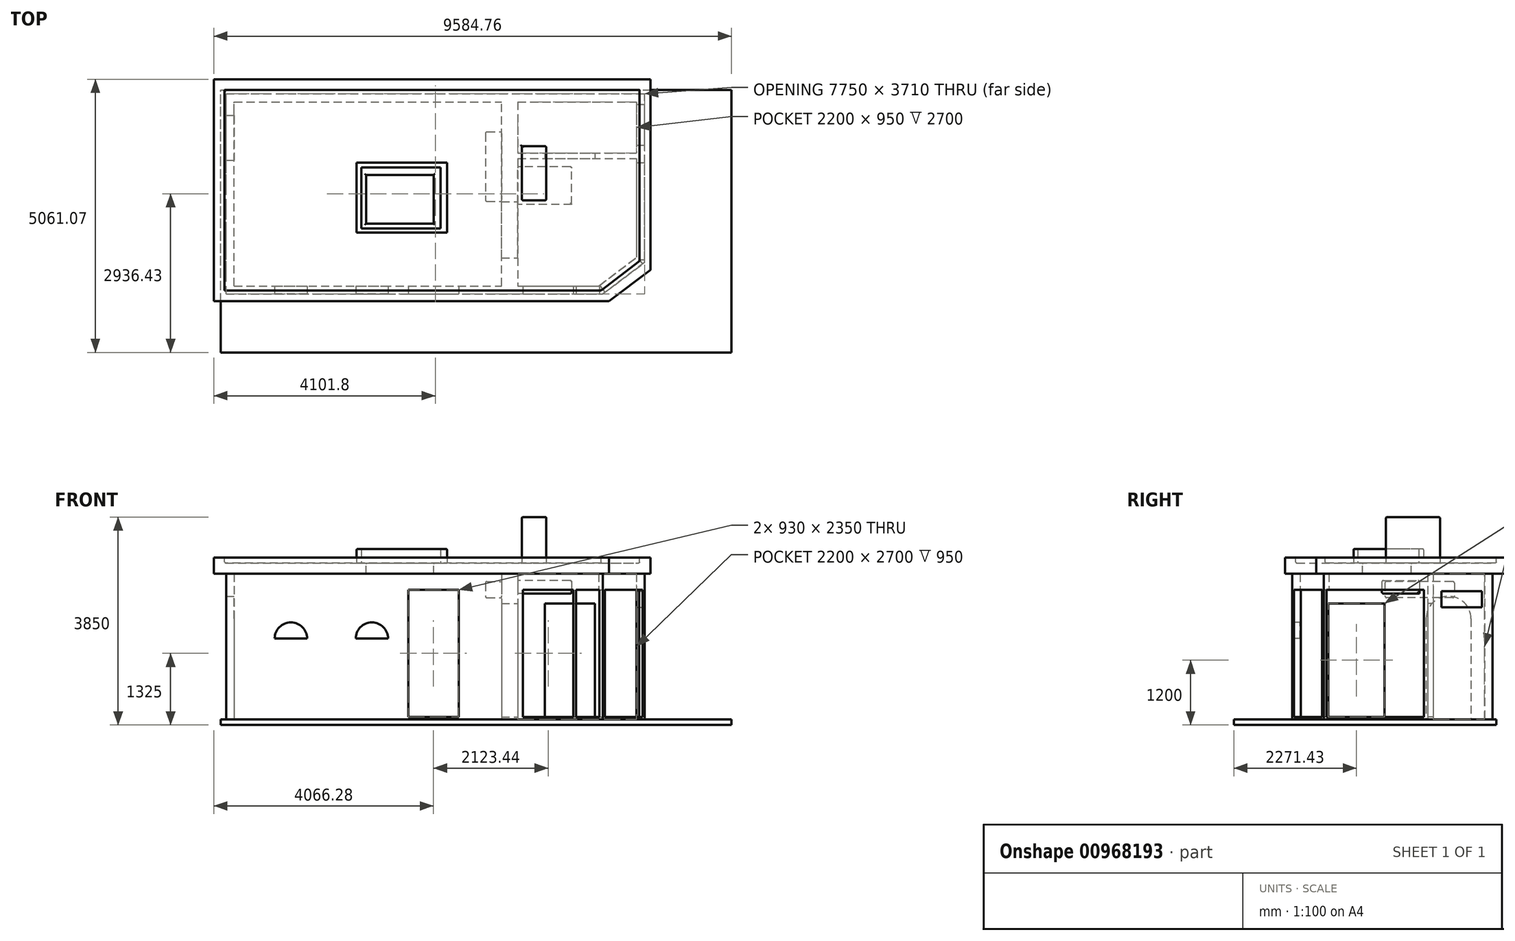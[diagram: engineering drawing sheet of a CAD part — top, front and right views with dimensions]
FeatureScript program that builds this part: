
annotation { "Feature Type Name" : "Feature", "Feature Type Description" : "" }
export const myFeature = defineFeature(function(context is Context, id is Id, definition is map)
    precondition{}
    {
        {
            var Q0;
            Q0=qCreatedBy(makeId("Top.planeOp"),FACE);
            var sketch = newSketch(context, id + "F0", { "sketchPlane" : qUnion([Q0])});
            skLineSegment(sketch, "E0.bottom", {"start": v(-3940.68, -1155.16) * mm, "end": v(1009.32, -1155.16) * mm});
            skLineSegment(sketch, "E0.top", {"start": v(-3940.68, 2254.84) * mm, "end": v(1009.32, 2254.84) * mm});
            skLineSegment(sketch, "E0.left", {"start": v(-3940.68, -1155.16) * mm, "end": v(-3940.68, 2254.84) * mm});
            skLineSegment(sketch, "E0.right", {"start": v(1009.32, -1155.16) * mm, "end": v(1009.32, 2254.84) * mm});
            skLineSegment(sketch, "E1.bottom", {"start": v(1309.32, 2254.84) * mm, "end": v(3509.32, 2254.84) * mm});
            skLineSegment(sketch, "E1.top", {"start": v(1309.32, -1155.16) * mm, "end": v(2809.32, -1155.16) * mm});
            skLineSegment(sketch, "E1.left", {"start": v(1309.32, 2254.84) * mm, "end": v(1309.32, -1155.16) * mm});
            skLineSegment(sketch, "E1.right", {"start": v(3509.32, 2254.84) * mm, "end": v(3509.32, -625.16) * mm});
            skLineSegment(sketch, "E2.bottom", {"start": v(-4090.68, -1305.16) * mm, "end": v(2885, -1305.16) * mm});
            skLineSegment(sketch, "E2.top", {"start": v(-4090.68, 2404.84) * mm, "end": v(3659.32, 2404.84) * mm});
            skLineSegment(sketch, "E2.left", {"start": v(-4090.68, -1305.16) * mm, "end": v(-4090.68, 2404.84) * mm});
            skLineSegment(sketch, "E2.right", {"start": v(3659.32, -718.9) * mm, "end": v(3659.32, 2404.84) * mm});
            skLineSegment(sketch, "E3", {"start": v(2809.32, -1155.16) * mm, "end": v(3509.32, -625.16) * mm});
            skPoint(sketch, "E4.orphan", {"position": v(3509.32, -1155.16) * mm});
            skLineSegment(sketch, "E5.bottom", {"start": v(1309.32, 1304.84) * mm, "end": v(1809.32, 1304.84) * mm});
            skLineSegment(sketch, "E5.top", {"start": v(1309.32, 1204.84) * mm, "end": v(1809.32, 1204.84) * mm});
            skLineSegment(sketch, "E5.left", {"start": v(1309.32, 1304.84) * mm, "end": v(1309.32, 1204.84) * mm});
            skLineSegment(sketch, "E6.right", {"start": v(3509.32, 1304.84) * mm, "end": v(3509.32, 1204.84) * mm});
            skPoint(sketch, "E7.orphan", {"position": v(1809.32, 1359.23) * mm});
            skLineSegment(sketch, "E8", {"start": v(3659.32, -718.9) * mm, "end": v(2885, -1305.16) * mm});
            skPoint(sketch, "E9.right.end.orphan", {"position": v(2739.32, 1204.84) * mm});
            skLineSegment(sketch, "E10", {"start": v(1809.32, 1304.84) * mm, "end": v(3509.32, 1304.84) * mm});
            skLineSegment(sketch, "E11", {"start": v(3509.32, 1204.84) * mm, "end": v(1809.32, 1204.84) * mm});
            skSolve(sketch);
        }
        {
            var Q0;
            Q0=makeQuery(id+"F0.imprint","IMPRINT",FACE,{"disambiguationData":[TD([[makeQuery(id+"F0.imprint","IMPRINT",EDGE,{"derivedFrom":sQuery(id+"F0.wireOp",EDGE,"E0.bottom")}),-1.0]])]});
            var Q1;
            Q1=makeQuery(id+"F0.imprint","IMPRINT",FACE,{"disambiguationData":[TD([[makeQuery(id+"F0.imprint","IMPRINT",EDGE,{"derivedFrom":sQuery(id+"F0.wireOp",EDGE,"E5.bottom")}),-1.0]])]});
            var Q2;
            Q2=makeQuery(id+"F0.imprint","IMPRINT",FACE,{"disambiguationData":[TD([[makeQuery(id+"F0.imprint","IMPRINT",EDGE,{"derivedFrom":sQuery(id+"F0.wireOp",EDGE,"E6.bottom")}),-1.0]])]});
            extrude(context, id + "F1", {"entities" : qUnion([Q0, Q1, Q2]), "depth" : 2700 * mm, "offsetDistance" : 25 * mm});
        }
        {
            var Q0;
            Q0=makeQuery(id+"F1.opExtrude","SWEPT_FACE",FACE,{"disambiguationData":[OSD([sQuery(id+"F0.wireOp",EDGE,"E2.bottom")])]});
            var sketch = newSketch(context, id + "F2", { "sketchPlane" : qUnion([Q0])});
            skLineSegment(sketch, "E12", {"start": v(-4012.93, 1500) * mm, "end": v(-3190.68, 1500) * mm, "construction": true});
            skArc(sketch, "E13", {"start": v(-2590.68, 1500) * mm, "mid": v(-2890.68, 1800) * mm, "end": v(-3190.68, 1500) * mm});
            skLineSegment(sketch, "E14", {"start": v(-3190.68, 1500) * mm, "end": v(-2590.68, 1500) * mm, "construction": true});
            skLineSegment(sketch, "E15", {"start": v(-2590.68, 1500) * mm, "end": v(902.67, 1500) * mm, "construction": true});
            skArc(sketch, "E16", {"start": v(-1090.68, 1500) * mm, "mid": v(-1390.68, 1800) * mm, "end": v(-1690.68, 1500) * mm});
            skLineSegment(sketch, "E17", {"start": v(-3190.68, 1500) * mm, "end": v(-2590.68, 1500) * mm});
            skLineSegment(sketch, "E18", {"start": v(-1690.68, 1500) * mm, "end": v(-1090.68, 1500) * mm});
            skLineSegment(sketch, "E19.bottom", {"start": v(-716.2, 2400) * mm, "end": v(213.8, 2400) * mm});
            skLineSegment(sketch, "E19.top", {"start": v(-716.2, 50) * mm, "end": v(213.8, 50) * mm});
            skLineSegment(sketch, "E19.left", {"start": v(-716.2, 2400) * mm, "end": v(-716.2, 50) * mm});
            skLineSegment(sketch, "E19.right", {"start": v(213.8, 2400) * mm, "end": v(213.8, 50) * mm});
            skLineSegment(sketch, "E20.bottom", {"start": v(1407.24, 2400) * mm, "end": v(2337.24, 2400) * mm});
            skLineSegment(sketch, "E20.top", {"start": v(1407.24, 50) * mm, "end": v(2337.24, 50) * mm});
            skLineSegment(sketch, "E20.left", {"start": v(1407.24, 2400) * mm, "end": v(1407.24, 50) * mm});
            skLineSegment(sketch, "E20.right", {"start": v(2337.24, 2400) * mm, "end": v(2337.24, 50) * mm});
            skLineSegment(sketch, "E21.bottom", {"start": v(2387.24, 2400) * mm, "end": v(2822.09, 2400) * mm});
            skLineSegment(sketch, "E21.top", {"start": v(2387.24, 50) * mm, "end": v(2822.09, 50) * mm});
            skLineSegment(sketch, "E21.left", {"start": v(2387.24, 2400) * mm, "end": v(2387.24, 50) * mm});
            skLineSegment(sketch, "E21.right", {"start": v(2822.09, 2400) * mm, "end": v(2822.09, 50) * mm});
            skSolve(sketch);
        }
        {
            var Q0;
            Q0=makeQuery(id+"F2.imprint","IMPRINT",FACE,{"disambiguationData":[TD([[makeQuery(id+"F2.imprint","IMPRINT",EDGE,{"derivedFrom":sQuery(id+"F2.wireOp",EDGE,"E16")}),1.0]])]});
            var Q1;
            Q1=makeQuery(id+"F2.imprint","IMPRINT",FACE,{"disambiguationData":[TD([[makeQuery(id+"F2.imprint","IMPRINT",EDGE,{"derivedFrom":sQuery(id+"F2.wireOp",EDGE,"E13")}),1.0]])]});
            var Q2;
            Q2=makeQuery(id+"F2.imprint","IMPRINT",FACE,{"disambiguationData":[TD([[makeQuery(id+"F2.imprint","IMPRINT",EDGE,{"derivedFrom":sQuery(id+"F2.wireOp",EDGE,"E19.bottom")}),-1.0]])]});
            var Q3;
            Q3=makeQuery(id+"F2.imprint","IMPRINT",FACE,{"disambiguationData":[TD([[makeQuery(id+"F2.imprint","IMPRINT",EDGE,{"derivedFrom":sQuery(id+"F2.wireOp",EDGE,"E21.bottom")}),-1.0]])]});
            var Q4;
            Q4=makeQuery(id+"F2.imprint","IMPRINT",FACE,{"disambiguationData":[TD([[makeQuery(id+"F2.imprint","IMPRINT",EDGE,{"derivedFrom":sQuery(id+"F2.wireOp",EDGE,"E20.bottom")}),-1.0]])]});
            extrude(context, id + "F3", {"entities" : qUnion([Q0, Q1, Q2, Q3, Q4]), "operationType" : NewBodyOperationType.REMOVE, "endBound" : BoundingType.UP_TO_NEXT, "oppositeDirection" : true, "depth" : 25 * mm, "offsetDistance" : 25 * mm});
        }
        {
            var Q0;
            Q0=makeQuery(id+"F1.opExtrude","SWEPT_FACE",FACE,{"disambiguationData":[OSD([sQuery(id+"F0.wireOp",EDGE,"E8")])]});
            var sketch = newSketch(context, id + "F4", { "sketchPlane" : qUnion([Q0])});
            skLineSegment(sketch, "E22.bottom", {"start": v(1562.25, 2400) * mm, "end": v(2433.47, 2400) * mm});
            skLineSegment(sketch, "E22.top", {"start": v(1562.25, 50) * mm, "end": v(2433.47, 50) * mm});
            skLineSegment(sketch, "E22.left", {"start": v(1562.25, 2400) * mm, "end": v(1562.25, 50) * mm});
            skLineSegment(sketch, "E22.right", {"start": v(2433.47, 2400) * mm, "end": v(2433.47, 50) * mm});
            skSolve(sketch);
        }
        {
            var Q0;
            Q0=makeQuery(id+"F4.imprint","IMPRINT",FACE,{"disambiguationData":[TD([[makeQuery(id+"F4.imprint","IMPRINT",EDGE,{"derivedFrom":sQuery(id+"F4.wireOp",EDGE,"E22.bottom")}),-1.0]])]});
            extrude(context, id + "F5", {"entities" : qUnion([Q0]), "operationType" : NewBodyOperationType.REMOVE, "endBound" : BoundingType.UP_TO_NEXT, "oppositeDirection" : true, "depth" : 25 * mm, "offsetDistance" : 25 * mm});
        }
        {
            var Q0;
            Q0=makeQuery(id+"F1.opExtrude","SWEPT_FACE",FACE,{"disambiguationData":[OSD([sQuery(id+"F0.wireOp",EDGE,"E2.right")])]});
            var sketch = newSketch(context, id + "F6", { "sketchPlane" : qUnion([Q0])});
            skLineSegment(sketch, "E23.bottom", {"start": v(-668.9, 2400) * mm, "end": v(1131.1, 2400) * mm});
            skLineSegment(sketch, "E23.top", {"start": v(-668.9, 50) * mm, "end": v(1131.1, 50) * mm});
            skLineSegment(sketch, "E23.left", {"start": v(-668.9, 2400) * mm, "end": v(-668.9, 50) * mm});
            skLineSegment(sketch, "E23.right", {"start": v(1131.1, 2400) * mm, "end": v(1131.1, 50) * mm});
            skSolve(sketch);
        }
        {
            var Q0;
            Q0=makeQuery(id+"F6.imprint","IMPRINT",FACE,{"disambiguationData":[TD([[makeQuery(id+"F6.imprint","IMPRINT",EDGE,{"derivedFrom":sQuery(id+"F6.wireOp",EDGE,"E23.bottom")}),-1.0]])]});
            extrude(context, id + "F7", {"entities" : qUnion([Q0]), "operationType" : NewBodyOperationType.REMOVE, "endBound" : BoundingType.UP_TO_NEXT, "oppositeDirection" : true, "depth" : 25 * mm, "offsetDistance" : 25 * mm});
        }
        {
            var Q0;
            {var subQ0=sQuery(id+"F0.wireOp",EDGE,"E1.left");Q0=makeQuery(id+"F1.opExtrude","SWEPT_FACE",FACE,{"disambiguationData":[OSD([subQ0]),TDD([makeQuery(id+"F0.imprint","IMPRINT",EDGE,{"disambiguationData":[TD([[makeQuery(id+"F0.imprint","INTERSECT",VERTEX,{"derivedFrom":[sQuery(id+"F0.wireOp",EDGE,"E1.top"),subQ0]}),1.0]])],"derivedFrom":subQ0})])]});}
            var sketch = newSketch(context, id + "F8", { "sketchPlane" : qUnion([Q0])});
            skLineSegment(sketch, "E24.bottom", {"start": v(-635.16, 2150) * mm, "end": v(404.84, 2150) * mm});
            skLineSegment(sketch, "E24.top", {"start": v(-635.16, 50) * mm, "end": v(404.84, 50) * mm});
            skLineSegment(sketch, "E24.left", {"start": v(-635.16, 2150) * mm, "end": v(-635.16, 50) * mm});
            skLineSegment(sketch, "E24.right", {"start": v(404.84, 2150) * mm, "end": v(404.84, 50) * mm});
            skSolve(sketch);
        }
        {
            var Q0;
            Q0=makeQuery(id+"F8.imprint","IMPRINT",FACE,{"disambiguationData":[TD([[makeQuery(id+"F8.imprint","IMPRINT",EDGE,{"derivedFrom":sQuery(id+"F8.wireOp",EDGE,"E24.bottom")}),-1.0]])]});
            extrude(context, id + "F9", {"entities" : qUnion([Q0]), "operationType" : NewBodyOperationType.REMOVE, "endBound" : BoundingType.UP_TO_NEXT, "oppositeDirection" : true, "depth" : 25 * mm, "offsetDistance" : 25 * mm});
        }
        {
            var Q0;
            Q0=makeQuery(id+"F1.opExtrude","SWEPT_FACE",FACE,{"disambiguationData":[OSD([sQuery(id+"F0.wireOp",EDGE,"E0.left")])]});
            var sketch = newSketch(context, id + "F10", { "sketchPlane" : qUnion([Q0])});
            skLineSegment(sketch, "E25.top", {"start": v(1174.84, -230.95) * mm, "end": v(2004.84, -230.95) * mm});
            skLineSegment(sketch, "E25.left", {"start": v(1174.84, 1869.05) * mm, "end": v(1174.84, -230.95) * mm});
            skLineSegment(sketch, "E25.right", {"start": v(2004.84, 1869.05) * mm, "end": v(2004.84, -230.95) * mm});
            skArc(sketch, "E26", {"start": v(2004.84, 1869.05) * mm, "mid": v(1589.84, 2284.05) * mm, "end": v(1174.84, 1869.05) * mm});
            skSolve(sketch);
        }
        {
            var Q0;
            Q0=makeQuery(id+"F10.imprint","IMPRINT",FACE,{"disambiguationData":[TD([[makeQuery(id+"F10.imprint","IMPRINT",EDGE,{"derivedFrom":sQuery(id+"F10.wireOp",EDGE,"E25.bottom")}),-1.0]])]});
            var Q1;
            {var subQ0=sQuery(id+"F10.wireOp",EDGE,"E26");Q1=makeQuery(id+"F10.imprint","IMPRINT",FACE,{"disambiguationData":[TD([[makeQuery(id+"F10.imprint","IMPRINT",EDGE,{"derivedFrom":subQ0}),1.0]])]});}
            extrude(context, id + "F11", {"entities" : qUnion([Q0, Q1]), "operationType" : NewBodyOperationType.REMOVE, "endBound" : BoundingType.UP_TO_NEXT, "oppositeDirection" : true, "depth" : 25 * mm, "offsetDistance" : 25 * mm});
        }
        {
            var Q0;
            Q0=makeQuery(id+"F1.opExtrude","SWEPT_FACE",FACE,{"disambiguationData":[OSD([sQuery(id+"F0.wireOp",EDGE,"E5.top"),sQuery(id+"F0.wireOp",EDGE,"E11")])]});
            var sketch = newSketch(context, id + "F12", { "sketchPlane" : qUnion([Q0])});
            skLineSegment(sketch, "E27.bottom", {"start": v(1809.32, 2150) * mm, "end": v(2739.32, 2150) * mm});
            skLineSegment(sketch, "E27.top", {"start": v(1809.32, 50) * mm, "end": v(2739.32, 50) * mm});
            skLineSegment(sketch, "E27.left", {"start": v(1809.32, 2150) * mm, "end": v(1809.32, 50) * mm});
            skLineSegment(sketch, "E27.right", {"start": v(2739.32, 2150) * mm, "end": v(2739.32, 50) * mm});
            skSolve(sketch);
        }
        {
            var Q0;
            Q0=makeQuery(id+"F12.imprint","IMPRINT",FACE,{"disambiguationData":[TD([[makeQuery(id+"F12.imprint","IMPRINT",EDGE,{"derivedFrom":sQuery(id+"F12.wireOp",EDGE,"E27.bottom")}),-1.0]])]});
            extrude(context, id + "F13", {"entities" : qUnion([Q0]), "operationType" : NewBodyOperationType.REMOVE, "endBound" : BoundingType.UP_TO_NEXT, "oppositeDirection" : true, "depth" : 25 * mm, "offsetDistance" : 25 * mm});
        }
        {
            var Q0;
            {var subQ0=sQuery(id+"F0.wireOp",EDGE,"E1.left");Q0=makeQuery(id+"F1.opExtrude","SWEPT_FACE",FACE,{"disambiguationData":[OSD([subQ0]),TDD([makeQuery(id+"F0.imprint","IMPRINT",EDGE,{"disambiguationData":[TD([[makeQuery(id+"F0.imprint","INTERSECT",VERTEX,{"derivedFrom":[sQuery(id+"F0.wireOp",EDGE,"E1.top"),subQ0]}),1.0]])],"derivedFrom":subQ0})])]});}
            var sketch = newSketch(context, id + "F14", { "sketchPlane" : qUnion([Q0])});
            skLineSegment(sketch, "E28.bottom", {"start": v(354.15, 2574.71) * mm, "end": v(1054.15, 2574.71) * mm});
            skLineSegment(sketch, "E28.top", {"start": v(354.15, 2334.71) * mm, "end": v(1054.15, 2334.71) * mm});
            skLineSegment(sketch, "E28.left", {"start": v(354.15, 2574.71) * mm, "end": v(354.15, 2334.71) * mm});
            skLineSegment(sketch, "E28.right", {"start": v(1054.15, 2574.71) * mm, "end": v(1054.15, 2334.71) * mm});
            skSolve(sketch);
        }
        {
            var Q0;
            Q0 = qSketchRegion(id + "F14", true);
            extrude(context, id + "F15", {"entities" : qUnion([Q0]), "operationType" : NewBodyOperationType.ADD, "depth" : 1000 * mm, "offsetDistance" : 25 * mm});
        }
        {
            var Q0;
            Q0=makeQuery(id+"F1.opExtrude","SWEPT_FACE",FACE,{"disambiguationData":[OSD([sQuery(id+"F0.wireOp",EDGE,"E0.right")])]});
            var sketch = newSketch(context, id + "F16", { "sketchPlane" : qUnion([Q0])});
            skLineSegment(sketch, "E29.bottom", {"start": v(-1696.84, 2556.84) * mm, "end": v(-413.2, 2556.84) * mm});
            skLineSegment(sketch, "E29.top", {"start": v(-1696.84, 2256.84) * mm, "end": v(-413.2, 2256.84) * mm});
            skLineSegment(sketch, "E29.left", {"start": v(-1696.84, 2556.84) * mm, "end": v(-1696.84, 2256.84) * mm});
            skLineSegment(sketch, "E29.right", {"start": v(-413.2, 2556.84) * mm, "end": v(-413.2, 2256.84) * mm});
            skSolve(sketch);
        }
        {
            var Q0;
            Q0 = qSketchRegion(id + "F16", true);
            extrude(context, id + "F17", {"entities" : qUnion([Q0]), "operationType" : NewBodyOperationType.ADD, "depth" : 300 * mm, "offsetDistance" : 25 * mm});
        }
        {
            var Q0;
            Q0=makeQuery(id+"F1.opExtrude","CAP_FACE",FACE,{"disambiguationData":[OSD([sQuery(id+"F0.wireOp",EDGE,"E0.bottom"),sQuery(id+"F0.wireOp",EDGE,"E0.top"),sQuery(id+"F0.wireOp",EDGE,"E0.left"),sQuery(id+"F0.wireOp",EDGE,"E0.right"),sQuery(id+"F0.wireOp",EDGE,"E1.bottom"),sQuery(id+"F0.wireOp",EDGE,"E1.top"),sQuery(id+"F0.wireOp",EDGE,"E1.left"),sQuery(id+"F0.wireOp",EDGE,"E1.right"),sQuery(id+"F0.wireOp",EDGE,"E2.bottom"),sQuery(id+"F0.wireOp",EDGE,"E2.top"),sQuery(id+"F0.wireOp",EDGE,"E2.left"),sQuery(id+"F0.wireOp",EDGE,"E2.right"),sQuery(id+"F0.wireOp",EDGE,"E3"),sQuery(id+"F0.wireOp",EDGE,"E5.bottom"),sQuery(id+"F0.wireOp",EDGE,"E5.top"),sQuery(id+"F0.wireOp",EDGE,"E8"),sQuery(id+"F0.wireOp",EDGE,"E10"),sQuery(id+"F0.wireOp",EDGE,"E11")])],"isStart":true});
            var sketch = newSketch(context, id + "F18", { "sketchPlane" : qUnion([Q0])});
            skLineSegment(sketch, "E30.bottom", {"start": v(-4191.62, 2386.59) * mm, "end": v(5267.28, 2386.59) * mm});
            skLineSegment(sketch, "E30.top", {"start": v(-4191.62, -2473.84) * mm, "end": v(5267.28, -2473.84) * mm});
            skLineSegment(sketch, "E30.left", {"start": v(-4191.62, 2386.59) * mm, "end": v(-4191.62, -2473.84) * mm});
            skLineSegment(sketch, "E30.right", {"start": v(5267.28, 2386.59) * mm, "end": v(5267.28, -2473.84) * mm});
            skSolve(sketch);
        }
        {
            var Q0;
            Q0 = qSketchRegion(id + "F18", true);
            extrude(context, id + "F19", {"entities" : qUnion([Q0]), "operationType" : NewBodyOperationType.ADD, "depth" : 100 * mm, "offsetDistance" : 25 * mm});
        }
        {
            var Q0;
            Q0=makeQuery(id+"F1.opExtrude","SWEPT_FACE",FACE,{"disambiguationData":[OSD([sQuery(id+"F0.wireOp",EDGE,"E2.right")])]});
            var sketch = newSketch(context, id + "F20", { "sketchPlane" : qUnion([Q0])});
            skLineSegment(sketch, "E31.bottom", {"start": v(1455.37, 2377.26) * mm, "end": v(2205.37, 2377.26) * mm});
            skLineSegment(sketch, "E31.top", {"start": v(1455.37, 2077.26) * mm, "end": v(2205.37, 2077.26) * mm});
            skLineSegment(sketch, "E31.left", {"start": v(1455.37, 2377.26) * mm, "end": v(1455.37, 2077.26) * mm});
            skLineSegment(sketch, "E31.right", {"start": v(2205.37, 2377.26) * mm, "end": v(2205.37, 2077.26) * mm});
            skSolve(sketch);
        }
        {
            var Q0;
            Q0=makeQuery(id+"F20.imprint","IMPRINT",FACE,{"disambiguationData":[TD([[makeQuery(id+"F20.imprint","IMPRINT",EDGE,{"derivedFrom":sQuery(id+"F20.wireOp",EDGE,"E31.bottom")}),-1.0]])]});
            extrude(context, id + "F21", {"entities" : qUnion([Q0]), "operationType" : NewBodyOperationType.REMOVE, "endBound" : BoundingType.UP_TO_NEXT, "oppositeDirection" : true, "depth" : 25 * mm, "offsetDistance" : 25 * mm});
        }
        {
            var Q0;
            Q0=makeQuery(id+"F15.opExtrude","SWEPT_EDGE",EDGE,{"disambiguationData":[OSD([sQuery(id+"F14.wireOp",EDGE,"E28.bottom"),sQuery(id+"F14.wireOp",EDGE,"E28.left")])]});
            var Q1;
            Q1=makeQuery(id+"F15.opExtrude","SWEPT_EDGE",EDGE,{"disambiguationData":[OSD([sQuery(id+"F14.wireOp",EDGE,"E28.top"),sQuery(id+"F14.wireOp",EDGE,"E28.left")])]});
            var Q2;
            Q2=makeQuery(id+"F15.opExtrude","CAP_EDGE",EDGE,{"disambiguationData":[OSD([sQuery(id+"F14.wireOp",EDGE,"E28.bottom")])],"isStart":false});
            var Q3;
            Q3=makeQuery(id+"F15.opExtrude","CAP_EDGE",EDGE,{"disambiguationData":[OSD([sQuery(id+"F14.wireOp",EDGE,"E28.top")])],"isStart":false});
            var Q4;
            Q4=makeQuery(id+"F15.opExtrude","CAP_EDGE",EDGE,{"disambiguationData":[OSD([sQuery(id+"F14.wireOp",EDGE,"E28.bottom")])],"isStart":true});
            var Q5;
            Q5=makeQuery(id+"F15.opExtrude","SWEPT_EDGE",EDGE,{"disambiguationData":[OSD([sQuery(id+"F14.wireOp",EDGE,"E28.bottom"),sQuery(id+"F14.wireOp",EDGE,"E28.right")])]});
            var Q6;
            Q6=makeQuery(id+"F15.opExtrude","CAP_EDGE",EDGE,{"disambiguationData":[OSD([sQuery(id+"F14.wireOp",EDGE,"E28.right")])],"isStart":false});
            fillet(context, id + "F22", {"entities" : qUnion([Q0, Q1, Q2, Q3, Q4, Q5, Q6]), "radius" : 30 * mm, "tangentPropagation" : true, "allowEdgeOverflow" : false});
        }
        {
            var Q0;
            Q0=makeQuery(id+"F17.opExtrude","CAP_EDGE",EDGE,{"disambiguationData":[OSD([sQuery(id+"F16.wireOp",EDGE,"E29.bottom")])],"isStart":false});
            var Q1;
            Q1=makeQuery(id+"F17.opExtrude","CAP_EDGE",EDGE,{"disambiguationData":[OSD([sQuery(id+"F16.wireOp",EDGE,"E29.top")])],"isStart":false});
            var Q2;
            Q2=makeQuery(id+"F17.opExtrude","CAP_EDGE",EDGE,{"disambiguationData":[OSD([sQuery(id+"F16.wireOp",EDGE,"E29.left")])],"isStart":false});
            var Q3;
            Q3=makeQuery(id+"F17.opExtrude","CAP_EDGE",EDGE,{"disambiguationData":[OSD([sQuery(id+"F16.wireOp",EDGE,"E29.right")])],"isStart":false});
            var Q4;
            Q4=makeQuery(id+"F17.opExtrude","SWEPT_EDGE",EDGE,{"disambiguationData":[OSD([sQuery(id+"F16.wireOp",EDGE,"E29.bottom"),sQuery(id+"F16.wireOp",EDGE,"E29.right")])]});
            var Q5;
            Q5=makeQuery(id+"F17.opExtrude","SWEPT_EDGE",EDGE,{"disambiguationData":[OSD([sQuery(id+"F16.wireOp",EDGE,"E29.top"),sQuery(id+"F16.wireOp",EDGE,"E29.right")])]});
            var Q6;
            Q6=makeQuery(id+"F17.opExtrude","SWEPT_EDGE",EDGE,{"disambiguationData":[OSD([sQuery(id+"F16.wireOp",EDGE,"E29.bottom"),sQuery(id+"F16.wireOp",EDGE,"E29.left")])]});
            var Q7;
            Q7=makeQuery(id+"F17.opExtrude","SWEPT_EDGE",EDGE,{"disambiguationData":[OSD([sQuery(id+"F16.wireOp",EDGE,"E29.top"),sQuery(id+"F16.wireOp",EDGE,"E29.left")])]});
            fillet(context, id + "F23", {"entities" : qUnion([Q0, Q1, Q2, Q3, Q4, Q5, Q6, Q7]), "radius" : 30 * mm, "tangentPropagation" : true, "allowEdgeOverflow" : false});
        }
        {
            var Q0;
            Q0=makeQuery(id+"F1.opExtrude","CAP_FACE",FACE,{"disambiguationData":[OSD([sQuery(id+"F0.wireOp",EDGE,"E0.bottom"),sQuery(id+"F0.wireOp",EDGE,"E0.top"),sQuery(id+"F0.wireOp",EDGE,"E0.left"),sQuery(id+"F0.wireOp",EDGE,"E0.right"),sQuery(id+"F0.wireOp",EDGE,"E1.bottom"),sQuery(id+"F0.wireOp",EDGE,"E1.top"),sQuery(id+"F0.wireOp",EDGE,"E1.left"),sQuery(id+"F0.wireOp",EDGE,"E1.right"),sQuery(id+"F0.wireOp",EDGE,"E2.bottom"),sQuery(id+"F0.wireOp",EDGE,"E2.top"),sQuery(id+"F0.wireOp",EDGE,"E2.left"),sQuery(id+"F0.wireOp",EDGE,"E2.right"),sQuery(id+"F0.wireOp",EDGE,"E3"),sQuery(id+"F0.wireOp",EDGE,"E5.bottom"),sQuery(id+"F0.wireOp",EDGE,"E5.top"),sQuery(id+"F0.wireOp",EDGE,"E8"),sQuery(id+"F0.wireOp",EDGE,"E10"),sQuery(id+"F0.wireOp",EDGE,"E11")])],"isStart":false});
            var sketch = newSketch(context, id + "F24", { "sketchPlane" : qUnion([Q0])});
            skLineSegment(sketch, "E32", {"start": v(-4317.48, 2674.48) * mm, "end": v(3766.53, 2674.48) * mm});
            skLineSegment(sketch, "E33", {"start": v(3766.53, 2674.48) * mm, "end": v(3766.53, -857.29) * mm});
            skLineSegment(sketch, "E34", {"start": v(3766.53, -857.29) * mm, "end": v(3001.18, -1439.27) * mm});
            skLineSegment(sketch, "E35", {"start": v(3001.18, -1439.27) * mm, "end": v(-4317.48, -1439.27) * mm});
            skLineSegment(sketch, "E36", {"start": v(-4317.48, -1439.27) * mm, "end": v(-4317.48, 2674.48) * mm});
            skSolve(sketch);
        }
        {
            var Q0;
            Q0 = qSketchRegion(id + "F24", true);
            extrude(context, id + "F25", {"entities" : qUnion([Q0]), "operationType" : NewBodyOperationType.ADD, "depth" : 300 * mm, "offsetDistance" : 25 * mm});
        }
        {
            var Q0;
            Q0=makeQuery(id+"F25.opExtrude","CAP_FACE",FACE,{"disambiguationData":[OSD([sQuery(id+"F24.wireOp",EDGE,"E32"),sQuery(id+"F24.wireOp",EDGE,"E33"),sQuery(id+"F24.wireOp",EDGE,"E34"),sQuery(id+"F24.wireOp",EDGE,"E35"),sQuery(id+"F24.wireOp",EDGE,"E36")])],"isStart":false});
            var sketch = newSketch(context, id + "F26", { "sketchPlane" : qUnion([Q0])});
            skLineSegment(sketch, "E37", {"start": v(-4117.48, 2474.48) * mm, "end": v(3566.53, 2474.48) * mm});
            skLineSegment(sketch, "E38", {"start": v(3566.53, 2474.48) * mm, "end": v(3566.53, -696.61) * mm});
            skLineSegment(sketch, "E39", {"start": v(1505.68, -1239.27) * mm, "end": v(-4117.48, -1239.27) * mm});
            skLineSegment(sketch, "E40", {"start": v(-4117.48, -1239.27) * mm, "end": v(-4117.48, 2474.48) * mm});
            skLineSegment(sketch, "E41", {"start": v(1505.68, -1239.27) * mm, "end": v(2852.9, -1239.27) * mm});
            skLineSegment(sketch, "E42", {"start": v(2852.9, -1239.27) * mm, "end": v(3566.53, -696.61) * mm});
            skSolve(sketch);
        }
        {
            var Q0;
            Q0=makeQuery(id+"F26.imprint","IMPRINT",FACE,{"disambiguationData":[TD([[makeQuery(id+"F26.imprint","IMPRINT",EDGE,{"derivedFrom":sQuery(id+"F26.wireOp",EDGE,"E37")}),-1.0]])]});
            extrude(context, id + "F27", {"entities" : qUnion([Q0]), "operationType" : NewBodyOperationType.REMOVE, "oppositeDirection" : true, "depth" : 100 * mm, "offsetDistance" : 25 * mm});
        }
        {
            var Q0;
            Q0=makeQuery(id+"F27.boolean.opBoolean","COPY",FACE,{"derivedFrom":makeQuery(id+"F27.opExtrude","CAP_FACE",FACE,{"disambiguationData":[OSD([sQuery(id+"F26.wireOp",EDGE,"E37"),sQuery(id+"F26.wireOp",EDGE,"E38"),sQuery(id+"F26.wireOp",EDGE,"E39"),sQuery(id+"F26.wireOp",EDGE,"E40"),sQuery(id+"F26.wireOp",EDGE,"E41"),sQuery(id+"F26.wireOp",EDGE,"E42")])],"isStart":false})});
            var sketch = newSketch(context, id + "F28", { "sketchPlane" : qUnion([Q0])});
            skLineSegment(sketch, "E43.bottom", {"start": v(1386.67, 1430.63) * mm, "end": v(1836.67, 1430.63) * mm});
            skLineSegment(sketch, "E43.top", {"start": v(1386.67, 430.63) * mm, "end": v(1836.67, 430.63) * mm});
            skLineSegment(sketch, "E43.left", {"start": v(1386.67, 1430.63) * mm, "end": v(1386.67, 430.63) * mm});
            skLineSegment(sketch, "E43.right", {"start": v(1836.67, 1430.63) * mm, "end": v(1836.67, 430.63) * mm});
            skCircle(sketch, "E44", {"center": v(822.26, 1826.4) * mm, "radius": 62.5 * mm});
            skSolve(sketch);
        }
        {
            var Q0;
            Q0=makeQuery(id+"F28.imprint","IMPRINT",FACE,{"disambiguationData":[TD([[makeQuery(id+"F28.imprint","IMPRINT",EDGE,{"derivedFrom":sQuery(id+"F28.wireOp",EDGE,"E43.bottom")}),-1.0]])]});
            extrude(context, id + "F29", {"entities" : qUnion([Q0]), "operationType" : NewBodyOperationType.ADD, "depth" : 850 * mm, "offsetDistance" : 25 * mm});
        }
        {
            var Q0;
            Q0=makeQuery(id+"F27.boolean.opBoolean","COPY",FACE,{"derivedFrom":makeQuery(id+"F27.opExtrude","CAP_FACE",FACE,{"disambiguationData":[OSD([sQuery(id+"F26.wireOp",EDGE,"E37"),sQuery(id+"F26.wireOp",EDGE,"E38"),sQuery(id+"F26.wireOp",EDGE,"E39"),sQuery(id+"F26.wireOp",EDGE,"E40"),sQuery(id+"F26.wireOp",EDGE,"E41"),sQuery(id+"F26.wireOp",EDGE,"E42")])],"isStart":false})});
            var sketch = newSketch(context, id + "F30", { "sketchPlane" : qUnion([Q0])});
            skCircle(sketch, "E45", {"center": v(1016.82, 1783.3) * mm, "radius": 62.5 * mm});
            skSolve(sketch);
        }
        {
            var Q0;
            Q0 = qSketchRegion(id + "F30", true);
            var Q1;
            Q1=sQuery(id+"F30.wireOp",EDGE,"E45");
            extrude(context, id + "F31", {"entities" : qUnion([Q0]), "bodyType" : ToolBodyType.SURFACE, "surfaceEntities" : qUnion([Q1]), "depth" : 300 * mm, "offsetDistance" : 25 * mm});
        }
        {
            var Q0;
            Q0=makeQuery(id+"F27.boolean.opBoolean","COPY",FACE,{"derivedFrom":makeQuery(id+"F27.opExtrude","CAP_FACE",FACE,{"disambiguationData":[OSD([sQuery(id+"F26.wireOp",EDGE,"E37"),sQuery(id+"F26.wireOp",EDGE,"E38"),sQuery(id+"F26.wireOp",EDGE,"E39"),sQuery(id+"F26.wireOp",EDGE,"E40"),sQuery(id+"F26.wireOp",EDGE,"E41"),sQuery(id+"F26.wireOp",EDGE,"E42")])],"isStart":false})});
            var sketch = newSketch(context, id + "F32", { "sketchPlane" : qUnion([Q0])});
            skLineSegment(sketch, "E46.bottom", {"start": v(-1498.85, 900) * mm, "end": v(-248.85, 900) * mm});
            skLineSegment(sketch, "E46.top", {"start": v(-1498.85, 0) * mm, "end": v(-248.85, 0) * mm});
            skLineSegment(sketch, "E46.left", {"start": v(-1498.85, 900) * mm, "end": v(-1498.85, 0) * mm});
            skLineSegment(sketch, "E46.right", {"start": v(-248.85, 900) * mm, "end": v(-248.85, 0) * mm});
            skSolve(sketch);
        }
        {
            var Q0;
            Q0 = qSketchRegion(id + "F32", true);
            extrude(context, id + "F33", {"entities" : qUnion([Q0]), "operationType" : NewBodyOperationType.REMOVE, "endBound" : BoundingType.UP_TO_NEXT, "oppositeDirection" : true, "depth" : 25 * mm, "offsetDistance" : 25 * mm});
        }
        {
            var Q0;
            Q0=makeQuery(id+"F27.boolean.opBoolean","COPY",FACE,{"derivedFrom":makeQuery(id+"F27.opExtrude","CAP_FACE",FACE,{"disambiguationData":[OSD([sQuery(id+"F26.wireOp",EDGE,"E37"),sQuery(id+"F26.wireOp",EDGE,"E38"),sQuery(id+"F26.wireOp",EDGE,"E39"),sQuery(id+"F26.wireOp",EDGE,"E40"),sQuery(id+"F26.wireOp",EDGE,"E41"),sQuery(id+"F26.wireOp",EDGE,"E42")])],"isStart":false})});
            var sketch = newSketch(context, id + "F34", { "sketchPlane" : qUnion([Q0])});
            skLineSegment(sketch, "E47.bottom", {"start": v(-1673.26, 1129.25) * mm, "end": v(0, 1129.25) * mm});
            skLineSegment(sketch, "E47.top", {"start": v(-1673.26, -168.32) * mm, "end": v(0, -168.32) * mm});
            skLineSegment(sketch, "E47.left", {"start": v(-1673.26, 1129.25) * mm, "end": v(-1673.26, -168.32) * mm});
            skLineSegment(sketch, "E47.right", {"start": v(0, 1129.25) * mm, "end": v(0, -168.32) * mm});
            skLineSegment(sketch, "E48.bottom", {"start": v(-1588.16, 1040.52) * mm, "end": v(-117.65, 1040.52) * mm});
            skLineSegment(sketch, "E48.top", {"start": v(-1588.16, -88.73) * mm, "end": v(-117.65, -88.73) * mm});
            skLineSegment(sketch, "E48.left", {"start": v(-1588.16, 1040.52) * mm, "end": v(-1588.16, -88.73) * mm});
            skLineSegment(sketch, "E48.right", {"start": v(-117.65, 1040.52) * mm, "end": v(-117.65, -88.73) * mm});
            skSolve(sketch);
        }
        {
            var Q0;
            Q0=makeQuery(id+"F34.imprint","IMPRINT",FACE,{"disambiguationData":[TD([[makeQuery(id+"F34.imprint","IMPRINT",EDGE,{"derivedFrom":sQuery(id+"F34.wireOp",EDGE,"E47.bottom")}),-1.0]])]});
            var Q1;
            Q1=sQuery(id+"F34.wireOp",EDGE,"E47.right");
            var Q2;
            Q2=sQuery(id+"F34.wireOp",EDGE,"E47.bottom");
            var Q3;
            Q3=sQuery(id+"F34.wireOp",EDGE,"E47.left");
            var Q4;
            Q4=sQuery(id+"F34.wireOp",EDGE,"E48.top");
            var Q5;
            Q5=sQuery(id+"F34.wireOp",EDGE,"E48.bottom");
            var Q6;
            Q6=sQuery(id+"F34.wireOp",EDGE,"E48.left");
            var Q7;
            Q7=sQuery(id+"F34.wireOp",EDGE,"E48.right");
            var Q8;
            Q8=sQuery(id+"F34.wireOp",EDGE,"E47.top");
            extrude(context, id + "F35", {"entities" : qUnion([Q0]), "surfaceEntities" : qUnion([Q1, Q2, Q3, Q4, Q5, Q6, Q7, Q8]), "depth" : 260 * mm, "offsetDistance" : 25 * mm});
        }
        {
            var Q0;
            Q0=makeQuery(id+"F35.opExtrude","CAP_EDGE",EDGE,{"disambiguationData":[OSD([sQuery(id+"F34.wireOp",EDGE,"E47.right")])],"isStart":false});
            var Q1;
            Q1=makeQuery(id+"F35.opExtrude","CAP_EDGE",EDGE,{"disambiguationData":[OSD([sQuery(id+"F34.wireOp",EDGE,"E47.top")])],"isStart":false});
            var Q2;
            Q2=makeQuery(id+"F35.opExtrude","CAP_EDGE",EDGE,{"disambiguationData":[OSD([sQuery(id+"F34.wireOp",EDGE,"E47.bottom")])],"isStart":false});
            var Q3;
            Q3=makeQuery(id+"F35.opExtrude","CAP_EDGE",EDGE,{"disambiguationData":[OSD([sQuery(id+"F34.wireOp",EDGE,"E47.left")])],"isStart":false});
            var Q4;
            Q4=makeQuery(id+"F29.opExtrude","CAP_EDGE",EDGE,{"disambiguationData":[OSD([sQuery(id+"F28.wireOp",EDGE,"E43.left")])],"isStart":false});
            var Q5;
            Q5=makeQuery(id+"F29.opExtrude","CAP_EDGE",EDGE,{"disambiguationData":[OSD([sQuery(id+"F28.wireOp",EDGE,"E43.top")])],"isStart":false});
            var Q6;
            Q6=makeQuery(id+"F29.opExtrude","CAP_FACE",FACE,{"disambiguationData":[OSD([sQuery(id+"F28.wireOp",EDGE,"E43.bottom"),sQuery(id+"F28.wireOp",EDGE,"E43.top"),sQuery(id+"F28.wireOp",EDGE,"E43.left"),sQuery(id+"F28.wireOp",EDGE,"E43.right")])],"isStart":false});
            var Q7;
            Q7=makeQuery(id+"F29.opExtrude","SWEPT_EDGE",EDGE,{"disambiguationData":[OSD([sQuery(id+"F28.wireOp",EDGE,"E43.top"),sQuery(id+"F28.wireOp",EDGE,"E43.right")])]});
            var Q8;
            Q8=makeQuery(id+"F29.opExtrude","SWEPT_EDGE",EDGE,{"disambiguationData":[OSD([sQuery(id+"F28.wireOp",EDGE,"E43.top"),sQuery(id+"F28.wireOp",EDGE,"E43.left")])]});
            var Q9;
            Q9=makeQuery(id+"F29.opExtrude","SWEPT_EDGE",EDGE,{"disambiguationData":[OSD([sQuery(id+"F28.wireOp",EDGE,"E43.bottom"),sQuery(id+"F28.wireOp",EDGE,"E43.right")])]});
            var Q10;
            Q10=makeQuery(id+"F27.boolean.opBoolean","COPY",FACE,{"derivedFrom":makeQuery(id+"F27.opExtrude","CAP_FACE",FACE,{"disambiguationData":[OSD([sQuery(id+"F26.wireOp",EDGE,"E37"),sQuery(id+"F26.wireOp",EDGE,"E38"),sQuery(id+"F26.wireOp",EDGE,"E39"),sQuery(id+"F26.wireOp",EDGE,"E40"),sQuery(id+"F26.wireOp",EDGE,"E41"),sQuery(id+"F26.wireOp",EDGE,"E42")])],"isStart":false})});
            fillet(context, id + "F36", {"entities" : qUnion([Q0, Q1, Q2, Q3, Q4, Q5, Q6, Q7, Q8, Q9, Q10]), "radius" : 20 * mm, "tangentPropagation" : true, "allowEdgeOverflow" : false});
        }
    });
